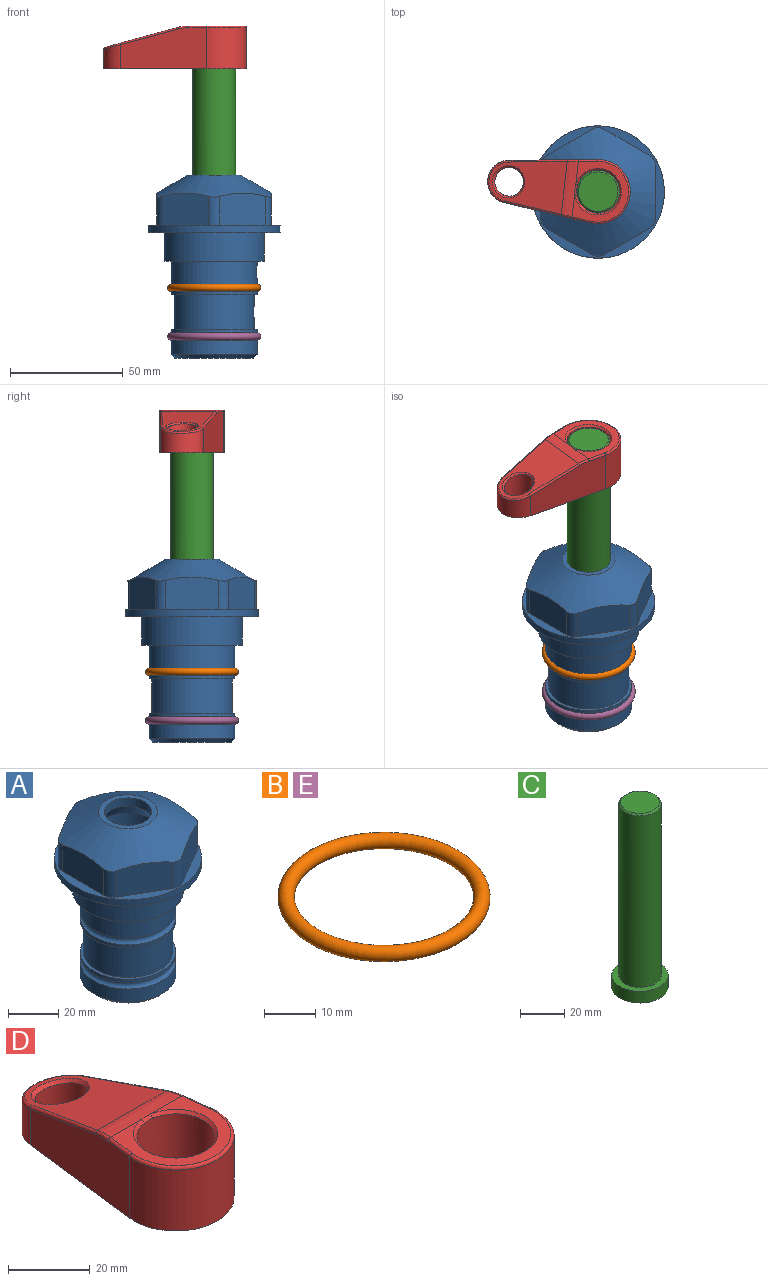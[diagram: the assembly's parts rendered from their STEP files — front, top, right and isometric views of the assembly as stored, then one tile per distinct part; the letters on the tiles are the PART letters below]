
ASSEMBLY  parts=5 mates=4
PART A: 36 faces, bbox 58.7x58.7x81 mm
  f0: cylinder r=17.78mm len=35.56mm, axis (0,0,1), area 1670.8mm2, adj f23,f24,f31
  f1: cylinder r=19.05mm len=38.1mm, axis (0,0,1), area 1191.9mm2, adj f26,f27,f30
  f2: plane 58.66x58.66mm, normal (0,0,-1), area 1150.6mm2, adj f3,f28
  f3: cylinder r=29.33mm len=58.66mm, axis (0,0,-1), area 585.1mm2, adj f2,f4
  f4: plane 58.66x58.66mm, normal (0,0,1), area 475.9mm2, adj f3,f5,f6,f7,f8,f9,f10,f11
  f5: plane 20.32x14.34mm, normal (-0.5,0.87,0), area 324.4mm2, adj f4,f15,f16,f17
  f6: plane 20.32x14.34mm, normal (0.5,0.87,0), area 324.4mm2, adj f4,f14,f15,f17
  f7: plane 23.48x14.34mm, normal (1,0,0), area 324.4mm2, adj f4,f13,f14,f17
  f8: plane 20.32x14.34mm, normal (0.5,-0.87,0), area 324.4mm2, adj f4,f12,f13,f17
  f9: plane 20.32x14.34mm, normal (-0.5,-0.87,0), area 324.4mm2, adj f4,f11,f12,f17
  f10: plane 23.48x14.34mm, normal (-1,0,0), area 324.4mm2, adj f4,f11,f16,f17
  f11: cylinder r=5.08mm len=12.85mm, axis (0,0,-1), area 67.2mm2, adj f4,f9,f10,f17
  f12: cylinder r=5.08mm len=12.85mm, axis (0,0,-1), area 67.2mm2, adj f4,f8,f9,f17
  f13: cylinder r=5.08mm len=12.85mm, axis (0,0,-1), area 67.2mm2, adj f4,f7,f8,f17
  f14: cylinder r=5.08mm len=12.85mm, axis (0,0,-1), area 67.2mm2, adj f4,f6,f7,f17
  f15: cylinder r=5.08mm len=12.85mm, axis (0,0,-1), area 67.2mm2, adj f4,f5,f6,f17
  f16: cylinder r=5.08mm len=12.85mm, axis (0,0,-1), area 67.2mm2, adj f4,f5,f10,f17
  f17: cone r=11.73mm half-angle=60deg, axis (0,0,-1), area 2071.8mm2, adj f5,f6,f7,f8,f9,f10,f11,f12
  f18: plane 23.46x23.46mm, normal (0,0,1), area 147.4mm2, adj f17,f35
  f19: plane 34.93x34.93mm, normal (0,0,-1), area 958mm2, adj f29
  f20: cylinder r=19.05mm len=38.1mm, axis (0,0,1), area 760.1mm2, adj f21,f29
  f21: torus R=19.05mm, axis (0,0,1), area 565.3mm2, adj f20,f22
  f22: cylinder r=19.05mm len=38.1mm, axis (0,0,1), area 190mm2, adj f21,f23
  f23: plane 38.1x38.1mm, normal (0,0,1), area 146.9mm2, adj f0,f22
  f24: plane 38.1x38.1mm, normal (0,0,-1), area 146.9mm2, adj f0,f25
  f25: cylinder r=19.05mm len=38.1mm, axis (0,0,1), area 190mm2, adj f24,f26
  f26: torus R=19.05mm, axis (0,0,1), area 565.3mm2, adj f1,f25
  f27: plane 44.45x44.45mm, normal (0,0,-1), area 411.7mm2, adj f1,f28
  f28: cylinder r=22.23mm len=44.45mm, axis (0,0,1), area 1773.5mm2, adj f2,f27
  f29: cone r=19.05mm half-angle=45deg, axis (0,0,1), area 257.5mm2, adj f19,f20
  f30: cylinder r=3.17mm len=6.75mm, axis (-1,0,0), area 128mm2, adj f1,f33
  f31: cylinder r=3.17mm len=6.35mm, axis (-1,0,0), area 102.5mm2, adj f0,f33
  f32: plane 25.4x25.4mm, normal (0,0,1), area 506.7mm2, adj f33
  f33: cylinder r=12.7mm len=66.42mm, axis (0,0,-1), area 5236.2mm2, adj f30,f31,f32,f34
  f34: cone r=9.53mm half-angle=30deg, axis (0,0,-1), area 443.4mm2, adj f33,f35
  f35: cylinder r=9.53mm len=19.05mm, axis (0,0,-1), area 240.9mm2, adj f18,f34
PART B: 1 faces, bbox 44.7x44.7x3.2 mm
  f0: torus R=19.05mm, axis (0,0,1), area 1193.9mm2
PART C: 6 faces, bbox 25.4x25.4x101.6 mm
  f0: plane 17.46x17.46mm, normal (0,0,1), area 239.5mm2, adj f5
  f1: plane 25.4x25.4mm, normal (0,0,-1), area 506.7mm2, adj f2
  f2: cylinder r=12.7mm len=25.4mm, axis (0,0,1), area 506.7mm2, adj f1,f3
  f3: plane 25.4x25.4mm, normal (0,0,1), area 221.7mm2, adj f2,f4
  f4: cylinder r=9.53mm len=94.46mm, axis (0,0,1), area 5653mm2, adj f3,f5
  f5: cone r=8.73mm half-angle=45deg, axis (0,0,-1), area 64.4mm2, adj f0,f4
PART D: 31 faces, bbox 31.7x65.5x19.8 mm
  f0: plane 39.12x18.26mm, normal (0.99,0.12,0), area 612.2mm2, adj f1,f4,f7,f11,f13,f15
  f1: cylinder r=9.53mm len=18.91mm, axis (0,0,-1), area 296.1mm2, adj f0,f2,f7,f17
  f2: plane 39.12x18.26mm, normal (-0.99,0.12,0), area 612.2mm2, adj f1,f4,f7,f12,f14,f16
  f3: cylinder r=6.35mm len=12.7mm, axis (0,0,-1), area 362.4mm2, adj f7,f18
  f4: cylinder r=14.29mm len=28.58mm, axis (0,0,-1), area 882.2mm2, adj f0,f2,f7,f10
  f5: cylinder r=9.53mm len=19.05mm, axis (0,0,-1), area 1092.6mm2, adj f7,f19,f20
  f6: plane 26.99x23.69mm, normal (0,0,1), area 216.2mm2, adj f9,f10,f11,f12,f19
  f7: plane 63.5x28.58mm, normal (0,0,-1), area 661.8mm2, adj f0,f1,f2,f3,f4,f5,f22,f23
  f8: plane 33.52x23.6mm, normal (0,0.26,0.97), area 486mm2, adj f9,f15,f16,f17,f18
  f9: cylinder r=19.05mm len=24.72mm, axis (1,0,0), area 120.4mm2, adj f6,f8,f13,f14,f20
  f10: torus R=13.49mm, axis (0,0,1), area 59mm2, adj f4,f6,f11,f12
  f11: cylinder r=0.79mm len=8.67mm, axis (0.12,-0.99,0), area 10.8mm2, adj f0,f6,f10,f13
  f12: cylinder r=0.79mm len=8.67mm, axis (0.12,0.99,0), area 10.8mm2, adj f2,f6,f10,f14
  f13: bspline ~4.95x1.42mm, area 6.1mm2, adj f0,f9,f11,f15
  f14: bspline ~4.95x1.42mm, area 6.1mm2, adj f2,f9,f12,f16
  f15: cylinder r=0.79mm len=25.95mm, axis (0.12,-0.96,0.26), area 32.9mm2, adj f0,f8,f13,f17
  f16: cylinder r=0.79mm len=25.95mm, axis (0.12,0.96,-0.26), area 32.9mm2, adj f2,f8,f14,f17
  f17: bspline ~18.91x8.38mm, area 30mm2, adj f1,f8,f15,f16
  f18: bspline ~14.29x14.29mm, area 48.3mm2, adj f3,f8
  f19: cone r=9.53mm half-angle=45deg, axis (0,0,1), area 66.5mm2, adj f5,f6,f20
  f20: bspline ~3.22x0.96mm, area 3.5mm2, adj f5,f9,f19
  f21: plane 2.75x2.72mm, normal (0,0,-1), area 2.9mm2, adj f23,f25,f28
  f22: plane 23.05x15.88mm, normal (-0.99,-0.12,0), area 323.6mm2, adj f7,f25,f26,f27,f28,f29
  f23: plane 23.05x15.88mm, normal (0.99,-0.12,0), area 323.6mm2, adj f7,f21,f25,f27,f28,f30
  f24: cylinder r=9.53mm len=10.69mm, axis (0,0,-1), area 114.7mm2, adj f7,f27,f29,f30
  f25: cylinder r=12.7mm len=20.59mm, axis (0,0,-1), area 381.1mm2, adj f7,f21,f22,f23,f26,f28
  f26: plane 2.75x2.72mm, normal (0,0,-1), area 2.9mm2, adj f22,f25,f28
  f27: plane 19.72x18.37mm, normal (0,-0.26,-0.97), area 291.8mm2, adj f22,f23,f24,f28,f29,f30
  f28: cylinder r=15.88mm len=19.92mm, axis (1,0,0), area 54.8mm2, adj f21,f22,f23,f25,f26,f27
  f29: cylinder r=1.59mm len=11mm, axis (0,0,-1), area 34.7mm2, adj f7,f22,f24,f27
  f30: cylinder r=1.59mm len=11mm, axis (0,0,-1), area 34.7mm2, adj f7,f23,f24,f27
PART E: same geometry as B
PLACE A at identity fixed
PLACE B at identity
PLACE C rot(axis=(0,0,1),83.6deg) t=(0,0,27.24)mm
PLACE D rot(axis=(0,0,1),83.6deg) t=(0,0,28.03)mm
PLACE E t=(0,0,-21.59)mm
MATE fastened B.f0 <-> A.f0  axis (0,0,1) through (0,0,-24.51)mm
MATE fastened C.f2 <-> D.f4  axis (0,0,1) through (0,0,90.74)mm
MATE cylindrical C.f2 <-> A.f0  axis (0,0,-1) through (0,0,-10.86)mm
MATE fastened E.f0 <-> A.f0  axis (0,0,1) through (0,0,-46.1)mm
